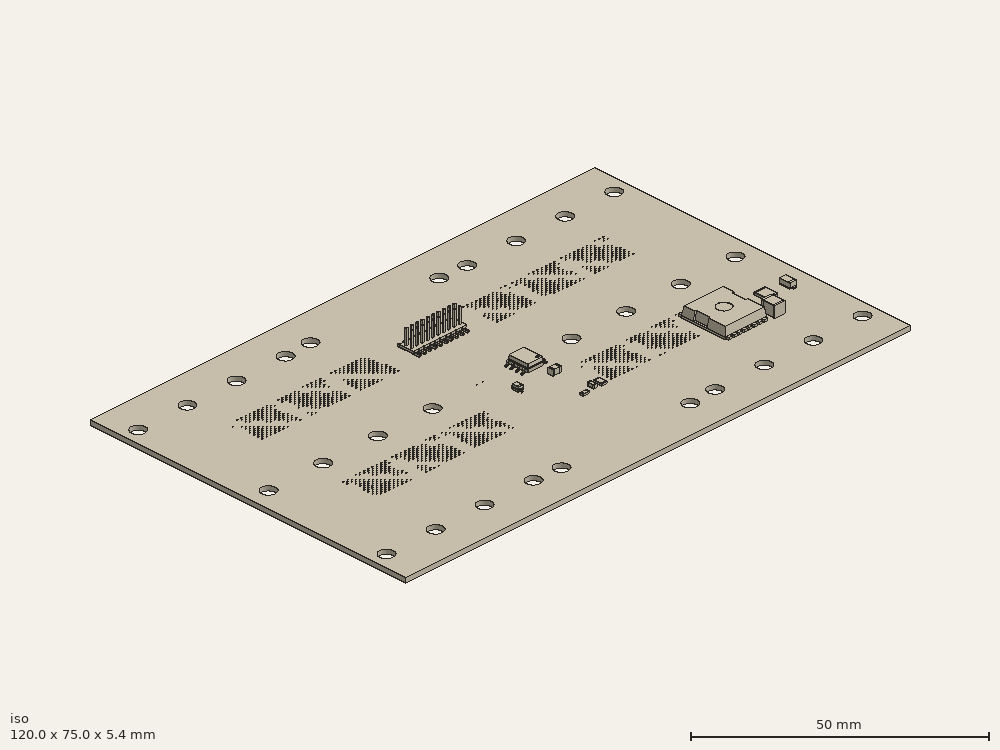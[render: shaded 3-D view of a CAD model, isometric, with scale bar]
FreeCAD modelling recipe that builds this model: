
FCSTD DOCUMENT  (FreeCAD 0.19R24291 (Git))
Label: switches
License: Creative Commons Attribution-NonCommercial-ShareAlike
LicenseURL: http://creativecommons.org/licenses/by-nc-sa/4.0/
objects: App::Link×92, PartDesign::Line×28, Part::Feature×12, App::LinkGroup×5, PartDesign::CoordinateSystem×2, Sketcher::SketchObject×1, App::Part×1
note: 43 computed .brp shape members not serialized (recipe doc carries the construction recipe); baked Part::Feature solids carry a one-line shape summary decoded from their .brp

FEATURE [PartDesign::CoordinateSystem] Local_CS_57a1
  AttacherType = Attacher::AttachEngine3D
FEATURE [Part::Feature] Pcb_57a1
  Placement = pos=(-102.25,63.55,0) rot=(0,0,1;0rad)
  shape: bbox 120 x 75 x 1 mm, 1846 faces (baked)
FEATURE [Sketcher::SketchObject] PCB_Sketch_57a1
  FullyConstrained = false
  sketch-geometry (4):
    g0: LineSegment StartX=120 StartY=0 StartZ=0 EndX=120 EndY=-75 EndZ=0
    g1: LineSegment StartX=0 StartY=0 StartZ=0 EndX=120 EndY=0 EndZ=0
    g2: LineSegment StartX=0 StartY=-75 StartZ=0 EndX=0 EndY=0 EndZ=0
    g3: LineSegment StartX=120 StartY=-75 StartZ=0 EndX=0 EndY=-75 EndZ=0
  constraints (4):
    c: Coincident(g2,g3)
    c: Coincident(g1,g2)
    c: Coincident(g0,g3)
    c: Coincident(g0,g1)
FEATURE [App::LinkGroup] Board_Geoms_57a1
  ElementList = -> [Pcb_57a1,Local_CS_57a1,PCB_Sketch_57a1]
  LinkMode = 0
FEATURE [Part::Feature] Shape  label="U102_SOIC_8_1EP_39x49mm_P127mm_606CF202"
  Placement = pos=(64.9625,-38.595,0) rot=(0,0,1;3.14159rad)
  shape: bbox 6 x 4.9 x 1.75 mm, 161 faces (baked)
FEATURE [App::Link] U102_SOIC_8_1EP_39x49mm_P127mm_606CF202_ln_  label="U101_SOIC_8_1EP_39x49mm_P127mm_60690A70"
  LinkPlacement = pos=(55,-38.65,0) rot=(0,0,1;0rad)
  LinkedObject = -> Shape
  Placement = pos=(55,-38.65,0) rot=(0,0,1;0rad)
FEATURE [Part::Feature] Shape001  label="Q112_Infineon_PG_HSOF_8_1_606C635D"
  Placement = pos=(99.55,-51.1,0) rot=(0,0,1;1.5708rad)
  shape: bbox 9.9 x 11.68 x 2.32 mm, 90 faces (baked)
FEATURE [App::Link] Q112_Infineon_PG_HSOF_8_1_606C635D_ln_  label="Q111_Infineon_PG_HSOF_8_1_606C5E26"
  LinkPlacement = pos=(87.875,-51.1,0) rot=(0,0,1;1.5708rad)
  LinkedObject = -> Shape001
  Placement = pos=(87.875,-51.1,0) rot=(0,0,1;1.5708rad)
FEATURE [App::Link] Q112_Infineon_PG_HSOF_8_1_606C635D_ln_001  label="Q110_Infineon_PG_HSOF_8_1_606C5F73"
  LinkPlacement = pos=(76.2,-51.1,0) rot=(0,0,1;1.5708rad)
  LinkedObject = -> Shape001
  Placement = pos=(76.2,-51.1,0) rot=(0,0,1;1.5708rad)
FEATURE [App::Link] Q112_Infineon_PG_HSOF_8_1_606C635D_ln_002  label="Q109_Infineon_PG_HSOF_8_1_60699C33"
  LinkPlacement = pos=(43.8,-51.1,0) rot=(0,0,1;1.5708rad)
  LinkedObject = -> Shape001
  Placement = pos=(43.8,-51.1,0) rot=(0,0,1;1.5708rad)
FEATURE [App::Link] Q112_Infineon_PG_HSOF_8_1_606C635D_ln_003  label="Q108_Infineon_PG_HSOF_8_1_60699B67"
  LinkPlacement = pos=(32.125,-51.1,0) rot=(0,0,1;1.5708rad)
  LinkedObject = -> Shape001
  Placement = pos=(32.125,-51.1,0) rot=(0,0,1;1.5708rad)
FEATURE [App::Link] Q112_Infineon_PG_HSOF_8_1_606C635D_ln_004  label="Q107_Infineon_PG_HSOF_8_1_60699CFF"
  LinkPlacement = pos=(20.45,-51.1,0) rot=(0,0,1;1.5708rad)
  LinkedObject = -> Shape001
  Placement = pos=(20.45,-51.1,0) rot=(0,0,1;1.5708rad)
FEATURE [App::Link] Q112_Infineon_PG_HSOF_8_1_606C635D_ln_005  label="Q106_Infineon_PG_HSOF_8_1_606C6210"
  LinkPlacement = pos=(99.55,-23.9,0) rot=(0,0,1;1.5708rad)
  LinkedObject = -> Shape001
  Placement = pos=(99.55,-23.9,0) rot=(0,0,1;1.5708rad)
FEATURE [App::Link] Q112_Infineon_PG_HSOF_8_1_606C635D_ln_006  label="Q105_Infineon_PG_HSOF_8_1_606C6780"
  LinkPlacement = pos=(87.875,-23.9,0) rot=(0,0,1;1.5708rad)
  LinkedObject = -> Shape001
  Placement = pos=(87.875,-23.9,0) rot=(0,0,1;1.5708rad)
FEATURE [App::Link] Q112_Infineon_PG_HSOF_8_1_606C635D_ln_007  label="Q104_Infineon_PG_HSOF_8_1_606C60C3"
  LinkPlacement = pos=(76.2,-23.9,0) rot=(0,0,1;1.5708rad)
  LinkedObject = -> Shape001
  Placement = pos=(76.2,-23.9,0) rot=(0,0,1;1.5708rad)
FEATURE [App::Link] Q112_Infineon_PG_HSOF_8_1_606C635D_ln_008  label="Q103_Infineon_PG_HSOF_8_1_605C8D17"
  LinkPlacement = pos=(43.8,-23.9,0) rot=(0,0,1;1.5708rad)
  LinkedObject = -> Shape001
  Placement = pos=(43.8,-23.9,0) rot=(0,0,1;1.5708rad)
FEATURE [App::Link] Q112_Infineon_PG_HSOF_8_1_606C635D_ln_009  label="Q102_Infineon_PG_HSOF_8_1_605C4D4F"
  LinkPlacement = pos=(32.125,-23.9,0) rot=(0,0,1;1.5708rad)
  LinkedObject = -> Shape001
  Placement = pos=(32.125,-23.9,0) rot=(0,0,1;1.5708rad)
FEATURE [App::Link] Q112_Infineon_PG_HSOF_8_1_606C635D_ln_010  label="Q101_Infineon_PG_HSOF_8_1_605C4D0A"
  LinkPlacement = pos=(20.45,-23.9,0) rot=(0,0,1;1.5708rad)
  LinkedObject = -> Shape001
  Placement = pos=(20.45,-23.9,0) rot=(0,0,1;1.5708rad)
FEATURE [Part::Feature] Shape002  label="Rsn108_R_1210_3225Metric_607492AA"
  Placement = pos=(109.97,-50.65,0) rot=(0,0,-1;1.5708rad)
  shape: bbox 2.5 x 3.2 x 0.55 mm, 26 faces (baked)
FEATURE [App::Link] Rsn108_R_1210_3225Metric_607492AA_ln_  label="Rsn107_R_1210_3225Metric_60749299"
  LinkPlacement = pos=(106.75,-50.65,0) rot=(0,0,-1;1.5708rad)
  LinkedObject = -> Shape002
  Placement = pos=(106.75,-50.65,0) rot=(0,0,-1;1.5708rad)
FEATURE [App::Link] Rsn108_R_1210_3225Metric_607492AA_ln_001  label="Rsn106_R_1210_3225Metric_60749288"
  LinkPlacement = pos=(10.05,-50.5,0) rot=(0,0,-1;1.5708rad)
  LinkedObject = -> Shape002
  Placement = pos=(10.05,-50.5,0) rot=(0,0,-1;1.5708rad)
FEATURE [App::Link] Rsn108_R_1210_3225Metric_607492AA_ln_002  label="Rsn105_R_1210_3225Metric_60749277"
  LinkPlacement = pos=(13.25,-50.5,0) rot=(0,0,-1;1.5708rad)
  LinkedObject = -> Shape002
  Placement = pos=(13.25,-50.5,0) rot=(0,0,-1;1.5708rad)
FEATURE [App::Link] Rsn108_R_1210_3225Metric_607492AA_ln_003  label="Rsn104_R_1210_3225Metric_60749266"
  LinkPlacement = pos=(109.95,-22.05,0) rot=(0,0,-1;1.5708rad)
  LinkedObject = -> Shape002
  Placement = pos=(109.95,-22.05,0) rot=(0,0,-1;1.5708rad)
FEATURE [App::Link] Rsn108_R_1210_3225Metric_607492AA_ln_004  label="Rsn102_R_1210_3225Metric_60749245"
  LinkPlacement = pos=(10.05,-22.05,0) rot=(0,0,-1;1.5708rad)
  LinkedObject = -> Shape002
  Placement = pos=(10.05,-22.05,0) rot=(0,0,-1;1.5708rad)
FEATURE [App::Link] Rsn108_R_1210_3225Metric_607492AA_ln_005  label="Rsn101_R_1210_3225Metric_60749234"
  LinkPlacement = pos=(13.25,-22.05,0) rot=(0,0,-1;1.5708rad)
  LinkedObject = -> Shape002
  Placement = pos=(13.25,-22.05,0) rot=(0,0,-1;1.5708rad)
FEATURE [Part::Feature] Shape003  label="Dsn108_D_SOD_123F_6074702B"
  Placement = pos=(115.15,-50.7,0) rot=(0,0,1;1.5708rad)
  shape: bbox 1.6 x 3.5 x 1.1 mm, 27 faces (baked)
FEATURE [App::Link] Dsn108_D_SOD_123F_6074702B_ln_  label="Dsn107_D_SOD_123F_60747012"
  LinkPlacement = pos=(112.8,-50.7,0) rot=(0,0,1;1.5708rad)
  LinkedObject = -> Shape003
  Placement = pos=(112.8,-50.7,0) rot=(0,0,1;1.5708rad)
FEATURE [App::Link] Dsn108_D_SOD_123F_6074702B_ln_001  label="Dsn106_D_SOD_123F_60746FF9"
  LinkPlacement = pos=(7.2,-50.6,0) rot=(0,0,1;1.5708rad)
  LinkedObject = -> Shape003
  Placement = pos=(7.2,-50.6,0) rot=(0,0,1;1.5708rad)
FEATURE [App::Link] Dsn108_D_SOD_123F_6074702B_ln_002  label="Dsn105_D_SOD_123F_60746FE0"
  LinkPlacement = pos=(4.85,-50.6,0) rot=(0,0,1;1.5708rad)
  LinkedObject = -> Shape003
  Placement = pos=(4.85,-50.6,0) rot=(0,0,1;1.5708rad)
FEATURE [App::Link] Dsn108_D_SOD_123F_6074702B_ln_003  label="Dsn104_D_SOD_123F_60746FC7"
  LinkPlacement = pos=(115.25,-22.05,0) rot=(0,0,1;1.5708rad)
  LinkedObject = -> Shape003
  Placement = pos=(115.25,-22.05,0) rot=(0,0,1;1.5708rad)
FEATURE [App::Link] Dsn108_D_SOD_123F_6074702B_ln_004  label="Dsn103_D_SOD_123F_60746FAE"
  LinkPlacement = pos=(112.85,-22.05,0) rot=(0,0,1;1.5708rad)
  LinkedObject = -> Shape003
  Placement = pos=(112.85,-22.05,0) rot=(0,0,1;1.5708rad)
FEATURE [App::Link] Dsn108_D_SOD_123F_6074702B_ln_005  label="Dsn102_D_SOD_123F_60746F95"
  LinkPlacement = pos=(7.25,-22,0) rot=(0,0,1;1.5708rad)
  LinkedObject = -> Shape003
  Placement = pos=(7.25,-22,0) rot=(0,0,1;1.5708rad)
FEATURE [App::Link] Dsn108_D_SOD_123F_6074702B_ln_006  label="Dsn101_D_SOD_123F_60746F7C"
  LinkPlacement = pos=(4.9,-22,0) rot=(0,0,1;1.5708rad)
  LinkedObject = -> Shape003
  Placement = pos=(4.9,-22,0) rot=(0,0,1;1.5708rad)
FEATURE [Part::Feature] Shape004  label="Csn108_C_1210_3225Metric_60746C07"
  Placement = pos=(106.75,-55.65,0) rot=(0,0,-1;1.5708rad)
  shape: bbox 2.5 x 3.2 x 2.5 mm, 28 faces (baked)
FEATURE [App::Link] Csn108_C_1210_3225Metric_60746C07_ln_  label="Csn107_C_1210_3225Metric_60746BF6"
  LinkPlacement = pos=(110,-55.65,0) rot=(0,0,-1;1.5708rad)
  LinkedObject = -> Shape004
  Placement = pos=(110,-55.65,0) rot=(0,0,-1;1.5708rad)
FEATURE [App::Link] Csn108_C_1210_3225Metric_60746C07_ln_001  label="Csn106_C_1210_3225Metric_60746BE5"
  LinkPlacement = pos=(10,-55.55,0) rot=(0,0,-1;1.5708rad)
  LinkedObject = -> Shape004
  Placement = pos=(10,-55.55,0) rot=(0,0,-1;1.5708rad)
FEATURE [App::Link] Csn108_C_1210_3225Metric_60746C07_ln_002  label="Csn105_C_1210_3225Metric_60746BD4"
  LinkPlacement = pos=(13.25,-55.55,0) rot=(0,0,-1;1.5708rad)
  LinkedObject = -> Shape004
  Placement = pos=(13.25,-55.55,0) rot=(0,0,-1;1.5708rad)
FEATURE [App::Link] Csn108_C_1210_3225Metric_60746C07_ln_003  label="Csn104_C_1210_3225Metric_60746BC3"
  LinkPlacement = pos=(109.95,-27.05,0) rot=(0,0,-1;1.5708rad)
  LinkedObject = -> Shape004
  Placement = pos=(109.95,-27.05,0) rot=(0,0,-1;1.5708rad)
FEATURE [App::Link] Csn108_C_1210_3225Metric_60746C07_ln_004  label="Csn102_C_1210_3225Metric_60746BA2"
  LinkPlacement = pos=(10.05,-27.05,0) rot=(0,0,-1;1.5708rad)
  LinkedObject = -> Shape004
  Placement = pos=(10.05,-27.05,0) rot=(0,0,-1;1.5708rad)
FEATURE [App::Link] Csn108_C_1210_3225Metric_60746C07_ln_005  label="Csn101_C_1210_3225Metric_60746B91"
  LinkPlacement = pos=(13.3,-27.05,0) rot=(0,0,-1;1.5708rad)
  LinkedObject = -> Shape004
  Placement = pos=(13.3,-27.05,0) rot=(0,0,-1;1.5708rad)
FEATURE [Part::Feature] Shape005  label="TH101_R_0805_2012Metric_606C0318"
  Placement = pos=(69.5,-51.775,0) rot=(0,0,1;1.5708rad)
  shape: bbox 1.2 x 2 x 0.45 mm, 26 faces (baked)
FEATURE [Part::Feature] Shape006  label="C111_C_0805_2012Metric_606CF1B7"
  Placement = pos=(66.425,-43.995,0) rot=(0,0,1;3.14159rad)
  shape: bbox 2 x 1.25 x 1.25 mm, 28 faces (baked)
FEATURE [App::Link] Csn108_C_1210_3225Metric_60746C07_ln_006  label="C110_C_1210_3225Metric_606CF49C"
  LinkPlacement = pos=(66.3625,-46.695,0) rot=(0,0,1;0rad)
  LinkedObject = -> Shape004
  Placement = pos=(66.3625,-46.695,0) rot=(0,0,1;0rad)
FEATURE [App::Link] Csn108_C_1210_3225Metric_60746C07_ln_007  label="C122_C_1210_3225Metric_606CF17E"
  LinkPlacement = pos=(64.8125,-32.795,0) rot=(0,0,-1;1.5708rad)
  LinkedObject = -> Shape004
  Placement = pos=(64.8125,-32.795,0) rot=(0,0,-1;1.5708rad)
FEATURE [Part::Feature] Shape007  label="C134_C_0603_1608Metric_606C0308"
  Placement = pos=(67.6,-51.75,0) rot=(0,0,1;1.5708rad)
  shape: bbox 0.8 x 1.6 x 0.8 mm, 28 faces (baked)
FEATURE [Part::Feature] Shape008  label="R117_R_0603_1608Metric_606C02F8"
  Placement = pos=(65,-52.575,0) rot=(0,0,1;0rad)
  shape: bbox 1.6 x 0.8 x 0.45 mm, 26 faces (baked)
FEATURE [Part::Feature] Shape009  label="D118_D_SOD_323_606ADB94"
  Placement = pos=(57.95,-43.65,0) rot=(0,0,1;1.5708rad)
  shape: bbox 1.25 x 2.5 x 1.1 mm, 67 faces (baked)
FEATURE [App::Link] R117_R_0603_1608Metric_606C02F8_ln_  label="R137_R_0603_1608Metric_606CF436"
  LinkPlacement = pos=(69.8125,-33.795,0) rot=(0,0,1;1.5708rad)
  LinkedObject = -> Shape008
  Placement = pos=(69.8125,-33.795,0) rot=(0,0,1;1.5708rad)
FEATURE [App::Link] R117_R_0603_1608Metric_606C02F8_ln_001  label="R136_R_0603_1608Metric_606AA3FF"
  LinkPlacement = pos=(50.15,-43.45,0) rot=(0,0,-1;1.5708rad)
  LinkedObject = -> Shape008
  Placement = pos=(50.15,-43.45,0) rot=(0,0,-1;1.5708rad)
FEATURE [App::Link] Dsn108_D_SOD_123F_6074702B_ln_007  label="D117_D_SOD_123F_606A943E"
  LinkPlacement = pos=(100.45,-56.45,-1) rot=(1,0,0;3.14159rad)
  LinkedObject = -> Shape003
  Placement = pos=(100.45,-56.45,-1) rot=(1,0,0;3.14159rad)
FEATURE [App::Link] Dsn108_D_SOD_123F_6074702B_ln_008  label="D116_D_SOD_123F_606A9425"
  LinkPlacement = pos=(88.775,-56.45,-1) rot=(1,0,0;3.14159rad)
  LinkedObject = -> Shape003
  Placement = pos=(88.775,-56.45,-1) rot=(1,0,0;3.14159rad)
FEATURE [App::Link] Dsn108_D_SOD_123F_6074702B_ln_009  label="D115_D_SOD_123F_606A940C"
  LinkPlacement = pos=(77.1,-56.45,-1) rot=(1,0,0;3.14159rad)
  LinkedObject = -> Shape003
  Placement = pos=(77.1,-56.45,-1) rot=(1,0,0;3.14159rad)
FEATURE [App::Link] D118_D_SOD_323_606ADB94_ln_  label="D114_D_SOD_323_606CF3BC"
  LinkPlacement = pos=(62.0125,-33.595,0) rot=(0,0,-1;1.5708rad)
  LinkedObject = -> Shape009
  Placement = pos=(62.0125,-33.595,0) rot=(0,0,-1;1.5708rad)
FEATURE [App::Link] Dsn108_D_SOD_123F_6074702B_ln_010  label="D113_D_SOD_123F_606A93DB"
  LinkPlacement = pos=(100.45,-29.25,-1) rot=(1,0,0;3.14159rad)
  LinkedObject = -> Shape003
  Placement = pos=(100.45,-29.25,-1) rot=(1,0,0;3.14159rad)
FEATURE [App::Link] Dsn108_D_SOD_123F_6074702B_ln_011  label="D112_D_SOD_123F_606A93C2"
  LinkPlacement = pos=(88.775,-29.25,-1) rot=(1,0,0;3.14159rad)
  LinkedObject = -> Shape003
  Placement = pos=(88.775,-29.25,-1) rot=(1,0,0;3.14159rad)
FEATURE [App::Link] Dsn108_D_SOD_123F_6074702B_ln_012  label="D111_D_SOD_123F_606CF303"
  LinkPlacement = pos=(67.8125,-33.395,0) rot=(0,0,1;1.5708rad)
  LinkedObject = -> Shape003
  Placement = pos=(67.8125,-33.395,0) rot=(0,0,1;1.5708rad)
FEATURE [App::Link] Dsn108_D_SOD_123F_6074702B_ln_013  label="D110_D_SOD_123F_606CF34B"
  LinkPlacement = pos=(70.0125,-41.95,0) rot=(0,0,-1;1.5708rad)
  LinkedObject = -> Shape003
  Placement = pos=(70.0125,-41.95,0) rot=(0,0,-1;1.5708rad)
FEATURE [App::Link] Dsn108_D_SOD_123F_6074702B_ln_014  label="D109_D_SOD_123F_606A9377"
  LinkPlacement = pos=(77.1,-29.25,-1) rot=(1,0,0;3.14159rad)
  LinkedObject = -> Shape003
  Placement = pos=(77.1,-29.25,-1) rot=(1,0,0;3.14159rad)
FEATURE [App::Link] Dsn108_D_SOD_123F_6074702B_ln_015  label="D108_D_SOD_123F_606A935E"
  LinkPlacement = pos=(44.7,-56.45,-1) rot=(1,0,0;3.14159rad)
  LinkedObject = -> Shape003
  Placement = pos=(44.7,-56.45,-1) rot=(1,0,0;3.14159rad)
FEATURE [App::Link] Dsn108_D_SOD_123F_6074702B_ln_016  label="D107_D_SOD_123F_606A9345"
  LinkPlacement = pos=(33.025,-56.45,-1) rot=(1,0,0;3.14159rad)
  LinkedObject = -> Shape003
  Placement = pos=(33.025,-56.45,-1) rot=(1,0,0;3.14159rad)
FEATURE [App::Link] Dsn108_D_SOD_123F_6074702B_ln_017  label="D106_D_SOD_123F_606A932C"
  LinkPlacement = pos=(21.35,-56.45,-1) rot=(1,0,0;3.14159rad)
  LinkedObject = -> Shape003
  Placement = pos=(21.35,-56.45,-1) rot=(1,0,0;3.14159rad)
FEATURE [App::Link] Dsn108_D_SOD_123F_6074702B_ln_018  label="D105_D_SOD_123F_606A9313"
  LinkPlacement = pos=(44.7,-29.25,-1) rot=(1,0,0;3.14159rad)
  LinkedObject = -> Shape003
  Placement = pos=(44.7,-29.25,-1) rot=(1,0,0;3.14159rad)
FEATURE [App::Link] Dsn108_D_SOD_123F_6074702B_ln_019  label="D104_D_SOD_123F_606A92FA"
  LinkPlacement = pos=(33.025,-29.25,-1) rot=(1,0,0;3.14159rad)
  LinkedObject = -> Shape003
  Placement = pos=(33.025,-29.25,-1) rot=(1,0,0;3.14159rad)
FEATURE [App::Link] Dsn108_D_SOD_123F_6074702B_ln_020  label="D103_D_SOD_123F_606A92E1"
  LinkPlacement = pos=(52.15,-43.85,0) rot=(0,0,-1;1.5708rad)
  LinkedObject = -> Shape003
  Placement = pos=(52.15,-43.85,0) rot=(0,0,-1;1.5708rad)
FEATURE [App::Link] Dsn108_D_SOD_123F_6074702B_ln_021  label="D102_D_SOD_123F_606A92C8"
  LinkPlacement = pos=(49.95,-35.25,0) rot=(0,0,1;1.5708rad)
  LinkedObject = -> Shape003
  Placement = pos=(49.95,-35.25,0) rot=(0,0,1;1.5708rad)
FEATURE [App::Link] Dsn108_D_SOD_123F_6074702B_ln_022  label="D101_D_SOD_123F_606A92AF"
  LinkPlacement = pos=(21.35,-29.25,-1) rot=(1,0,0;3.14159rad)
  LinkedObject = -> Shape003
  Placement = pos=(21.35,-29.25,-1) rot=(1,0,0;3.14159rad)
FEATURE [App::Link] C134_C_0603_1608Metric_606C0308_ln_  label="C196_C_0603_1608Metric_606CF2C2"
  LinkPlacement = pos=(66.2875,-42.195,0) rot=(0,0,1;3.14159rad)
  LinkedObject = -> Shape007
  Placement = pos=(66.2875,-42.195,0) rot=(0,0,1;3.14159rad)
FEATURE [App::Link] C134_C_0603_1608Metric_606C0308_ln_001  label="C195_C_0603_1608Metric_606A9285"
  LinkPlacement = pos=(53.6875,-35.05,0) rot=(0,0,1;0rad)
  LinkedObject = -> Shape007
  Placement = pos=(53.6875,-35.05,0) rot=(0,0,1;0rad)
FEATURE [App::Link] R117_R_0603_1608Metric_606C02F8_ln_002  label="R135_R_0603_1608Metric_606977C6"
  LinkPlacement = pos=(103.65,-55.65,-1) rot=(0.707107,0.707107,0;3.14159rad)
  LinkedObject = -> Shape008
  Placement = pos=(103.65,-55.65,-1) rot=(0.707107,0.707107,0;3.14159rad)
FEATURE [App::Link] R117_R_0603_1608Metric_606C02F8_ln_003  label="R134_R_0603_1608Metric_606977B5"
  LinkPlacement = pos=(91.975,-55.65,-1) rot=(0.707107,0.707107,0;3.14159rad)
  LinkedObject = -> Shape008
  Placement = pos=(91.975,-55.65,-1) rot=(0.707107,0.707107,0;3.14159rad)
FEATURE [App::Link] R117_R_0603_1608Metric_606C02F8_ln_004  label="R133_R_0603_1608Metric_606977A4"
  LinkPlacement = pos=(80.3,-55.65,-1) rot=(0.707107,0.707107,0;3.14159rad)
  LinkedObject = -> Shape008
  Placement = pos=(80.3,-55.65,-1) rot=(0.707107,0.707107,0;3.14159rad)
FEATURE [App::Link] R117_R_0603_1608Metric_606C02F8_ln_005  label="R132_R_0603_1608Metric_60697793"
  LinkPlacement = pos=(103.65,-28.45,-1) rot=(0.707107,0.707107,0;3.14159rad)
  LinkedObject = -> Shape008
  Placement = pos=(103.65,-28.45,-1) rot=(0.707107,0.707107,0;3.14159rad)
FEATURE [App::Link] R117_R_0603_1608Metric_606C02F8_ln_006  label="R131_R_0603_1608Metric_60697782"
  LinkPlacement = pos=(91.975,-28.45,-1) rot=(0.707107,0.707107,0;3.14159rad)
  LinkedObject = -> Shape008
  Placement = pos=(91.975,-28.45,-1) rot=(0.707107,0.707107,0;3.14159rad)
FEATURE [App::Link] R117_R_0603_1608Metric_606C02F8_ln_007  label="R130_R_0603_1608Metric_60697771"
  LinkPlacement = pos=(80.3,-28.45,-1) rot=(0.707107,0.707107,0;3.14159rad)
  LinkedObject = -> Shape008
  Placement = pos=(80.3,-28.45,-1) rot=(0.707107,0.707107,0;3.14159rad)
FEATURE [App::Link] R117_R_0603_1608Metric_606C02F8_ln_008  label="R129_R_0603_1608Metric_60697760"
  LinkPlacement = pos=(47.9,-55.65,-1) rot=(0.707107,0.707107,0;3.14159rad)
  LinkedObject = -> Shape008
  Placement = pos=(47.9,-55.65,-1) rot=(0.707107,0.707107,0;3.14159rad)
FEATURE [App::Link] R117_R_0603_1608Metric_606C02F8_ln_009  label="R128_R_0603_1608Metric_6069774F"
  LinkPlacement = pos=(36.225,-55.65,-1) rot=(0.707107,0.707107,0;3.14159rad)
  LinkedObject = -> Shape008
  Placement = pos=(36.225,-55.65,-1) rot=(0.707107,0.707107,0;3.14159rad)
FEATURE [App::Link] R117_R_0603_1608Metric_606C02F8_ln_010  label="R127_R_0603_1608Metric_6069773E"
  LinkPlacement = pos=(24.55,-55.65,-1) rot=(0.707107,0.707107,0;3.14159rad)
  LinkedObject = -> Shape008
  Placement = pos=(24.55,-55.65,-1) rot=(0.707107,0.707107,0;3.14159rad)
FEATURE [App::Link] R117_R_0603_1608Metric_606C02F8_ln_011  label="R126_R_0603_1608Metric_6069772D"
  LinkPlacement = pos=(47.9,-28.45,-1) rot=(0.707107,0.707107,0;3.14159rad)
  LinkedObject = -> Shape008
  Placement = pos=(47.9,-28.45,-1) rot=(0.707107,0.707107,0;3.14159rad)
FEATURE [App::Link] R117_R_0603_1608Metric_606C02F8_ln_012  label="R125_R_0603_1608Metric_6069771C"
  LinkPlacement = pos=(36.225,-28.45,-1) rot=(0.707107,0.707107,0;3.14159rad)
  LinkedObject = -> Shape008
  Placement = pos=(36.225,-28.45,-1) rot=(0.707107,0.707107,0;3.14159rad)
FEATURE [App::Link] R117_R_0603_1608Metric_606C02F8_ln_013  label="R124_R_0603_1608Metric_6069770B"
  LinkPlacement = pos=(24.55,-28.45,-1) rot=(0.707107,0.707107,0;3.14159rad)
  LinkedObject = -> Shape008
  Placement = pos=(24.55,-28.45,-1) rot=(0.707107,0.707107,0;3.14159rad)
FEATURE [App::Link] C134_C_0603_1608Metric_606C0308_ln_002  label="C131_C_0603_1608Metric_606DFE7B"
  LinkPlacement = pos=(51.3875,-21.85,0) rot=(0,0,1;3.14159rad)
  LinkedObject = -> Shape007
  Placement = pos=(51.3875,-21.85,0) rot=(0,0,1;3.14159rad)
FEATURE [App::Link] R117_R_0603_1608Metric_606C02F8_ln_014  label="R123_R_0603_1608Metric_606E087C"
  LinkPlacement = pos=(68.55,-19.15,0) rot=(0,0,1;0rad)
  LinkedObject = -> Shape008
  Placement = pos=(68.55,-19.15,0) rot=(0,0,1;0rad)
FEATURE [App::Link] R117_R_0603_1608Metric_606C02F8_ln_015  label="R122_R_0603_1608Metric_606E086B"
  LinkPlacement = pos=(68.55,-25.45,0) rot=(0,0,1;0rad)
  LinkedObject = -> Shape008
  Placement = pos=(68.55,-25.45,0) rot=(0,0,1;0rad)
FEATURE [App::Link] R117_R_0603_1608Metric_606C02F8_ln_016  label="R121_R_0603_1608Metric_606E085A"
  LinkPlacement = pos=(51.35,-23.55,0) rot=(0,0,1;3.14159rad)
  LinkedObject = -> Shape008
  Placement = pos=(51.35,-23.55,0) rot=(0,0,1;3.14159rad)
FEATURE [App::Link] R117_R_0603_1608Metric_606C02F8_ln_017  label="R120_R_0603_1608Metric_606E0849"
  LinkPlacement = pos=(68.55,-17.55,0) rot=(0,0,1;3.14159rad)
  LinkedObject = -> Shape008
  Placement = pos=(68.55,-17.55,0) rot=(0,0,1;3.14159rad)
FEATURE [App::Link] R117_R_0603_1608Metric_606C02F8_ln_018  label="R119_R_0603_1608Metric_606E0838"
  LinkPlacement = pos=(68.55,-27.05,0) rot=(0,0,1;3.14159rad)
  LinkedObject = -> Shape008
  Placement = pos=(68.55,-27.05,0) rot=(0,0,1;3.14159rad)
FEATURE [App::Link] R117_R_0603_1608Metric_606C02F8_ln_019  label="R118_R_0603_1608Metric_606E0827"
  LinkPlacement = pos=(51.3375,-25.25,0) rot=(0,0,1;0rad)
  LinkedObject = -> Shape008
  Placement = pos=(51.3375,-25.25,0) rot=(0,0,1;0rad)
FEATURE [App::Link] C134_C_0603_1608Metric_606C0308_ln_003  label="C133_C_0603_1608Metric_606DFE9D"
  LinkPlacement = pos=(68.5125,-20.75,0) rot=(0,0,1;0rad)
  LinkedObject = -> Shape007
  Placement = pos=(68.5125,-20.75,0) rot=(0,0,1;0rad)
FEATURE [App::Link] C134_C_0603_1608Metric_606C0308_ln_004  label="C132_C_0603_1608Metric_606DFE8C"
  LinkPlacement = pos=(68.5125,-23.75,0) rot=(0,0,1;0rad)
  LinkedObject = -> Shape007
  Placement = pos=(68.5125,-23.75,0) rot=(0,0,1;0rad)
FEATURE [App::Link] TH101_R_0805_2012Metric_606C0318_ln_  label="R114_R_0805_2012Metric_606C6A2D"
  LinkPlacement = pos=(72.75,-56.35,-1) rot=(1,0,0;3.14159rad)
  LinkedObject = -> Shape005
  Placement = pos=(72.75,-56.35,-1) rot=(1,0,0;3.14159rad)
FEATURE [App::Link] TH101_R_0805_2012Metric_606C0318_ln_001  label="R113_R_0805_2012Metric_606C69FD"
  LinkPlacement = pos=(96.1,-29.15,-1) rot=(1,0,0;3.14159rad)
  LinkedObject = -> Shape005
  Placement = pos=(96.1,-29.15,-1) rot=(1,0,0;3.14159rad)
FEATURE [App::Link] TH101_R_0805_2012Metric_606C0318_ln_002  label="R115_R_0805_2012Metric_606C69CD"
  LinkPlacement = pos=(84.4,-56.35,-1) rot=(1,0,0;3.14159rad)
  LinkedObject = -> Shape005
  Placement = pos=(84.4,-56.35,-1) rot=(1,0,0;3.14159rad)
FEATURE [App::Link] TH101_R_0805_2012Metric_606C0318_ln_003  label="R116_R_0805_2012Metric_606C699D"
  LinkPlacement = pos=(96.1,-56.35,-1) rot=(1,0,0;3.14159rad)
  LinkedObject = -> Shape005
  Placement = pos=(96.1,-56.35,-1) rot=(1,0,0;3.14159rad)
FEATURE [App::Link] TH101_R_0805_2012Metric_606C0318_ln_004  label="R103_R_0805_2012Metric_606863C2"
  LinkPlacement = pos=(17,-29.15,-1) rot=(1,0,0;3.14159rad)
  LinkedObject = -> Shape005
  Placement = pos=(17,-29.15,-1) rot=(1,0,0;3.14159rad)
FEATURE [App::Link] C111_C_0805_2012Metric_606CF1B7_ln_  label="C108_C_0805_2012Metric_60685BB9"
  LinkPlacement = pos=(53.55,-33.25,0) rot=(0,0,1;0rad)
  LinkedObject = -> Shape006
  Placement = pos=(53.55,-33.25,0) rot=(0,0,1;0rad)
FEATURE [App::Link] TH101_R_0805_2012Metric_606C0318_ln_005  label="R107_R_0805_2012Metric_60686406"
  LinkPlacement = pos=(28.675,-56.35,-1) rot=(1,0,0;3.14159rad)
  LinkedObject = -> Shape005
  Placement = pos=(28.675,-56.35,-1) rot=(1,0,0;3.14159rad)
FEATURE [App::Link] Csn108_C_1210_3225Metric_60746C07_ln_008  label="C107_C_1210_3225Metric_60685BA8"
  LinkPlacement = pos=(53.5875,-30.65,0) rot=(0,0,1;3.14159rad)
  LinkedObject = -> Shape004
  Placement = pos=(53.5875,-30.65,0) rot=(0,0,1;3.14159rad)
FEATURE [App::Link] TH101_R_0805_2012Metric_606C0318_ln_006  label="R104_R_0805_2012Metric_606863D3"
  LinkPlacement = pos=(28.675,-29.15,-1) rot=(1,0,0;3.14159rad)
  LinkedObject = -> Shape005
  Placement = pos=(28.675,-29.15,-1) rot=(1,0,0;3.14159rad)
FEATURE [App::Link] TH101_R_0805_2012Metric_606C0318_ln_007  label="R105_R_0805_2012Metric_606863E4"
  LinkPlacement = pos=(40.35,-29.15,-1) rot=(1,0,0;3.14159rad)
  LinkedObject = -> Shape005
  Placement = pos=(40.35,-29.15,-1) rot=(1,0,0;3.14159rad)
FEATURE [App::Link] Csn108_C_1210_3225Metric_60746C07_ln_009  label="Csn103_C_1210_3225Metric_606C66EB"
  LinkPlacement = pos=(106.65,-27.05,0) rot=(0,0,-1;1.5708rad)
  LinkedObject = -> Shape004
  Placement = pos=(106.65,-27.05,0) rot=(0,0,-1;1.5708rad)
FEATURE [Part::Feature] Shape010  label="J105_PinHeader_2x10_P127mm_Vertical_SMD_606D32DE"
  Placement = pos=(60,-21.5,0) rot=(0,0,1;1.5708rad)
  shape: bbox 12.7 x 5.57 x 4.4 mm, 444 faces (baked)
FEATURE [App::Link] TH101_R_0805_2012Metric_606C0318_ln_008  label="R112_R_0805_2012Metric_606C665B"
  LinkPlacement = pos=(84.425,-29.15,-1) rot=(1,0,0;3.14159rad)
  LinkedObject = -> Shape005
  Placement = pos=(84.425,-29.15,-1) rot=(1,0,0;3.14159rad)
FEATURE [App::Link] TH101_R_0805_2012Metric_606C0318_ln_009  label="R108_R_0805_2012Metric_60686417"
  LinkPlacement = pos=(40.35,-56.35,-1) rot=(1,0,0;3.14159rad)
  LinkedObject = -> Shape005
  Placement = pos=(40.35,-56.35,-1) rot=(1,0,0;3.14159rad)
FEATURE [App::Link] Csn108_C_1210_3225Metric_60746C07_ln_010  label="C109_C_1210_3225Metric_60685BCA"
  LinkPlacement = pos=(55.15,-44.45,0) rot=(0,0,1;1.5708rad)
  LinkedObject = -> Shape004
  Placement = pos=(55.15,-44.45,0) rot=(0,0,1;1.5708rad)
FEATURE [App::Link] Rsn108_R_1210_3225Metric_607492AA_ln_006  label="Rsn103_R_1210_3225Metric_606C659B"
  LinkPlacement = pos=(106.65,-22.05,0) rot=(0,0,-1;1.5708rad)
  LinkedObject = -> Shape002
  Placement = pos=(106.65,-22.05,0) rot=(0,0,-1;1.5708rad)
FEATURE [App::LinkGroup] Top_57a1
  ElementList = -> [Shape,U102_SOIC_8_1EP_39x49mm_P127mm_606CF202_ln_,Shape001,Q112_Infineon_PG_HSOF_8_1_606C635D_ln_,Q112_Infineon_PG_HSOF_8_1_606C635D_ln_001,Q112_Infineon_PG_HSOF_8_1_606C635D_ln_002,Q112_Infineon_PG_HSOF_8_1_606C635D_ln_003,Q112_Infineon_PG_HSOF_8_1_606C635D_ln_004,Q112_Infineon_PG_HSOF_8_1_606C635D_ln_005,Q112_Infineon_PG_HSOF_8_1_606C635D_ln_006,Q112_Infineon_PG_HSOF_8_1_606C635D_ln_007,+56 more]
  LinkMode = 0
FEATURE [App::Link] TH101_R_0805_2012Metric_606C0318_ln_010  label="R106_R_0805_2012Metric_606863F5"
  LinkPlacement = pos=(17,-56.35,-1) rot=(1,0,0;3.14159rad)
  LinkedObject = -> Shape005
  Placement = pos=(17,-56.35,-1) rot=(1,0,0;3.14159rad)
FEATURE [App::Link] TH101_R_0805_2012Metric_606C0318_ln_011  label="R111_R_0805_2012Metric_606C653B"
  LinkPlacement = pos=(72.75,-29.15,-1) rot=(1,0,0;3.14159rad)
  LinkedObject = -> Shape005
  Placement = pos=(72.75,-29.15,-1) rot=(1,0,0;3.14159rad)
FEATURE [App::LinkGroup] Bot_57a1
  ElementList = -> [Dsn108_D_SOD_123F_6074702B_ln_007,Dsn108_D_SOD_123F_6074702B_ln_008,Dsn108_D_SOD_123F_6074702B_ln_009,Dsn108_D_SOD_123F_6074702B_ln_010,Dsn108_D_SOD_123F_6074702B_ln_011,Dsn108_D_SOD_123F_6074702B_ln_014,Dsn108_D_SOD_123F_6074702B_ln_015,Dsn108_D_SOD_123F_6074702B_ln_016,Dsn108_D_SOD_123F_6074702B_ln_017,Dsn108_D_SOD_123F_6074702B_ln_018,Dsn108_D_SOD_123F_6074702B_ln_019,+25 more]
  LinkMode = 0
FEATURE [App::LinkGroup] Step_Models_57a1
  ElementList = -> [Top_57a1,Bot_57a1]
  LinkMode = 0
FEATURE [App::LinkGroup] Board_57a1  label="Switches"
  ElementList = -> [Board_Geoms_57a1,Step_Models_57a1]
  LinkMode = 0
FEATURE [PartDesign::CoordinateSystem] LCS_0
  AttacherType = Attacher::AttachEngine3D
  MapMode = 2
  Support = -> [X_Axis]
FEATURE [PartDesign::Line] HoleAxis_1
  AttacherType = Attacher::AttachEngineLine
  Length = 4.50902
  MapMode = 19
  Placement = pos=(3.4,-8,0) rot=(0,0,1;0rad)
  ResizeMode = 1
  Support = -> [Pcb_57a1]
FEATURE [PartDesign::Line] HoleAxis_2
  AttacherType = Attacher::AttachEngineLine
  Length = 4.50902
  MapMode = 19
  Placement = pos=(15.0667,-8,0) rot=(0,0,1;0rad)
  ResizeMode = 1
  Support = -> [Pcb_57a1]
FEATURE [PartDesign::Line] HoleAxis_3
  AttacherType = Attacher::AttachEngineLine
  Length = 4.50902
  MapMode = 19
  Placement = pos=(26.7333,-8,0) rot=(0,0,1;0rad)
  ResizeMode = 1
  Support = -> [Pcb_57a1]
FEATURE [PartDesign::Line] HoleAxis_4
  AttacherType = Attacher::AttachEngineLine
  Length = 4.50902
  MapMode = 19
  Placement = pos=(38.4,-8,0) rot=(0,0,1;0rad)
  ResizeMode = 1
  Support = -> [Pcb_57a1]
FEATURE [PartDesign::Line] HoleAxis_5
  AttacherType = Attacher::AttachEngineLine
  Length = 4.50902
  MapMode = 19
  Placement = pos=(44.62,-7.71,0) rot=(0,0,1;0rad)
  ResizeMode = 1
  Support = -> [Pcb_57a1]
FEATURE [PartDesign::Line] HoleAxis_6
  AttacherType = Attacher::AttachEngineLine
  Length = 4.50902
  MapMode = 19
  Placement = pos=(75.27,-7.69792,0) rot=(0,0,1;0rad)
  ResizeMode = 1
  Support = -> [Pcb_57a1]
FEATURE [PartDesign::Line] HoleAxis_7
  AttacherType = Attacher::AttachEngineLine
  Length = 4.50902
  MapMode = 19
  Placement = pos=(81.6,-8,0) rot=(0,0,1;0rad)
  ResizeMode = 1
  Support = -> [Pcb_57a1]
FEATURE [PartDesign::Line] HoleAxis_8
  AttacherType = Attacher::AttachEngineLine
  Length = 4.50902
  MapMode = 19
  Placement = pos=(93.2667,-8,0) rot=(0,0,1;0rad)
  ResizeMode = 1
  Support = -> [Pcb_57a1]
FEATURE [PartDesign::Line] HoleAxis_9
  AttacherType = Attacher::AttachEngineLine
  Length = 4.50902
  MapMode = 19
  Placement = pos=(104.933,-8,0) rot=(0,0,1;0rad)
  ResizeMode = 1
  Support = -> [Pcb_57a1]
FEATURE [PartDesign::Line] HoleAxis_10
  AttacherType = Attacher::AttachEngineLine
  Length = 4.50902
  MapMode = 19
  Placement = pos=(116.6,-8,0) rot=(0,0,1;0rad)
  ResizeMode = 1
  Support = -> [Pcb_57a1]
FEATURE [PartDesign::Line] HoleAxis_11
  AttacherType = Attacher::AttachEngineLine
  Length = 4.50902
  MapMode = 19
  Placement = pos=(115.55,-37.84,0) rot=(0,0,1;0rad)
  ResizeMode = 1
  Support = -> [Pcb_57a1]
FEATURE [PartDesign::Line] HoleAxis_12
  AttacherType = Attacher::AttachEngineLine
  Length = 4.50902
  MapMode = 19
  Placement = pos=(102.55,-37.84,0) rot=(0,0,1;0rad)
  ResizeMode = 1
  Support = -> [Pcb_57a1]
FEATURE [PartDesign::Line] HoleAxis_13
  AttacherType = Attacher::AttachEngineLine
  Length = 4.50902
  MapMode = 19
  Placement = pos=(89.55,-37.84,0) rot=(0,0,1;0rad)
  ResizeMode = 1
  Support = -> [Pcb_57a1]
FEATURE [PartDesign::Line] HoleAxis_14
  AttacherType = Attacher::AttachEngineLine
  Length = 4.50902
  MapMode = 19
  Placement = pos=(76.55,-37.84,0) rot=(0,0,1;0rad)
  ResizeMode = 1
  Support = -> [Pcb_57a1]
FEATURE [PartDesign::Line] HoleAxis_15
  AttacherType = Attacher::AttachEngineLine
  Length = 4.50902
  MapMode = 19
  Placement = pos=(43.45,-37.9,0) rot=(0,0,1;0rad)
  ResizeMode = 1
  Support = -> [Pcb_57a1]
FEATURE [PartDesign::Line] HoleAxis_16
  AttacherType = Attacher::AttachEngineLine
  Length = 4.50902
  MapMode = 19
  Placement = pos=(30.45,-37.9,0) rot=(0,0,1;0rad)
  ResizeMode = 1
  Support = -> [Pcb_57a1]
FEATURE [PartDesign::Line] HoleAxis_17
  AttacherType = Attacher::AttachEngineLine
  Length = 4.50902
  MapMode = 19
  Placement = pos=(17.45,-37.9,0) rot=(0,0,1;0rad)
  ResizeMode = 1
  Support = -> [Pcb_57a1]
FEATURE [PartDesign::Line] HoleAxis_18
  AttacherType = Attacher::AttachEngineLine
  Length = 4.50902
  MapMode = 19
  Placement = pos=(4.45,-37.9,0) rot=(0,0,1;0rad)
  ResizeMode = 1
  Support = -> [Pcb_57a1]
FEATURE [PartDesign::Line] HoleAxis_19
  AttacherType = Attacher::AttachEngineLine
  Length = 4.50902
  MapMode = 19
  Placement = pos=(15.0667,-67,0) rot=(0,0,1;0rad)
  ResizeMode = 1
  Support = -> [Pcb_57a1]
FEATURE [PartDesign::Line] HoleAxis_20
  AttacherType = Attacher::AttachEngineLine
  Length = 4.50902
  MapMode = 19
  Placement = pos=(26.7333,-67,0) rot=(0,0,1;0rad)
  ResizeMode = 1
  Support = -> [Pcb_57a1]
FEATURE [PartDesign::Line] HoleAxis_21
  AttacherType = Attacher::AttachEngineLine
  Length = 4.50902
  MapMode = 19
  Placement = pos=(38.4,-67,0) rot=(0,0,1;0rad)
  ResizeMode = 1
  Support = -> [Pcb_57a1]
FEATURE [PartDesign::Line] HoleAxis_22
  AttacherType = Attacher::AttachEngineLine
  Length = 4.50902
  MapMode = 19
  Placement = pos=(44.73,-67.3021,0) rot=(0,0,1;0rad)
  ResizeMode = 1
  Support = -> [Pcb_57a1]
FEATURE [PartDesign::Line] HoleAxis_23
  AttacherType = Attacher::AttachEngineLine
  Length = 4.50902
  MapMode = 19
  Placement = pos=(75.38,-67.29,0) rot=(0,0,1;0rad)
  ResizeMode = 1
  Support = -> [Pcb_57a1]
FEATURE [PartDesign::Line] HoleAxis_24
  AttacherType = Attacher::AttachEngineLine
  Length = 4.50902
  MapMode = 19
  Placement = pos=(81.6,-67,0) rot=(0,0,1;0rad)
  ResizeMode = 1
  Support = -> [Pcb_57a1]
FEATURE [PartDesign::Line] HoleAxis_25
  AttacherType = Attacher::AttachEngineLine
  Length = 4.50902
  MapMode = 19
  Placement = pos=(93.2667,-67,0) rot=(0,0,1;0rad)
  ResizeMode = 1
  Support = -> [Pcb_57a1]
FEATURE [PartDesign::Line] HoleAxis_26
  AttacherType = Attacher::AttachEngineLine
  Length = 4.50902
  MapMode = 19
  Placement = pos=(104.933,-67,0) rot=(0,0,1;0rad)
  ResizeMode = 1
  Support = -> [Pcb_57a1]
FEATURE [PartDesign::Line] HoleAxis_27
  AttacherType = Attacher::AttachEngineLine
  Length = 4.50902
  MapMode = 19
  Placement = pos=(116.6,-67,0) rot=(0,0,1;0rad)
  ResizeMode = 1
  Support = -> [Pcb_57a1]
FEATURE [PartDesign::Line] HoleAxis_28
  AttacherType = Attacher::AttachEngineLine
  Length = 4.50902
  MapMode = 19
  Placement = pos=(3.4,-67,0) rot=(0,0,1;0rad)
  ResizeMode = 1
  Support = -> [Pcb_57a1]
FEATURE [App::Part] Part
  Group = -> [LCS_0,Rsn108_R_1210_3225Metric_607492AA_ln_004,Rsn108_R_1210_3225Metric_607492AA_ln_003,Rsn108_R_1210_3225Metric_607492AA_ln_001,R117_R_0603_1608Metric_606C02F8_ln_017,Rsn108_R_1210_3225Metric_607492AA_ln_006,R117_R_0603_1608Metric_606C02F8_ln_018,R117_R_0603_1608Metric_606C02F8_ln_019,C134_C_0603_1608Metric_606C0308_ln_003,C134_C_0603_1608Metric_606C0308_ln_004,Dsn108_D_SOD_123F_6074702B_ln_021,+129 more]
  Origin = -> Origin
